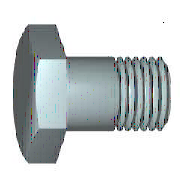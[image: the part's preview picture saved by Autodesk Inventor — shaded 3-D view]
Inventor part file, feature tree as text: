
AUTODESK INVENTOR PART (.ipt)
format: ipt  version: 2024.2 (Build 282272000, 272)  size: 203,776 bytes
history: native  units: mm (DEFAULTED — no unit token found)
features: other x4, plane x3, sketch x2, chamfer x1, fillet x1
ambient origin geometry x6: Origin, XY Plane, X Axis, Y Axis, Z Axis, Center Point
bodies: Solid1 (feature_tree)
feature tree (11):
  plane  "WorkPlane1"
  sketch  "Sketch1"  dims[d0=30.0mm]
  other  "WorkPoint1"
  chamfer  "Chamfer1"  Distance=15.0mm
  fillet  "Fillet1"  Radius=17.321016mm
  other  "MSC_A1"
  other  "MSC_PF1"
  other  "MSC_PT1"
  plane  "WorkPlane2"
  plane  "WorkPlane3"
  sketch  "Sketch2"  dims[d1=13.0mm d2=15.0mm d4=17.321016mm d6=5.3mm d7=0.0mm d8=15.0mm d10=0.0mm d12=30.0deg d14=360.0deg d15=0.0mm d17=10.0mm d18=4.0mm d19=80.0mm d20=16.0mm d21=360.0deg d22=0.625mm d23=0.625mm d24=0.4mm d25=0.1mm d26=0.0mm d27=60.0deg d28=6.5mm d29=0.0mm d30=0.0mm d32=0.0mm d33=0.0mm d34=0.0mm d37=0.0mm d38=0.0mm d39=45.0deg d40=0.0mm d41=0.0mm d42=0.0mm]
